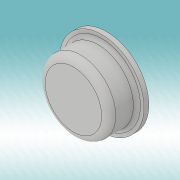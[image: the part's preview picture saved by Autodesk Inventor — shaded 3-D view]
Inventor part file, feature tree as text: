
AUTODESK INVENTOR PART (.ipt)
format: ipt  version: 2019 (Build 230136000, 136)  size: 138,240 bytes
history: native  units: mm
features: extrude x2, sketch x2, fillet x1
ambient origin geometry x8: Origin, YZ Plane, XZ Plane, XY Plane, X Axis, Y Axis, Z Axis, Center Point
bodies: Body1 (feature_tree)
feature tree (5):
  extrude  "Extrusion2"  Depth=8.0mm
  extrude  "Extrusion3"  Depth=0.5mm
  fillet  "Fillet1"  Radius=0.7mm
  sketch  "Sketch1"  dims[d0=16.0mm d1=8.0mm]
  sketch  "Sketch3"  dims[d2=8.0mm d3=12.0mm d7=0.7mm d8=0.0mm d10=10.0mm d11=4.0mm d12=0.0mm d13=1.0mm d14=0.5mm]
